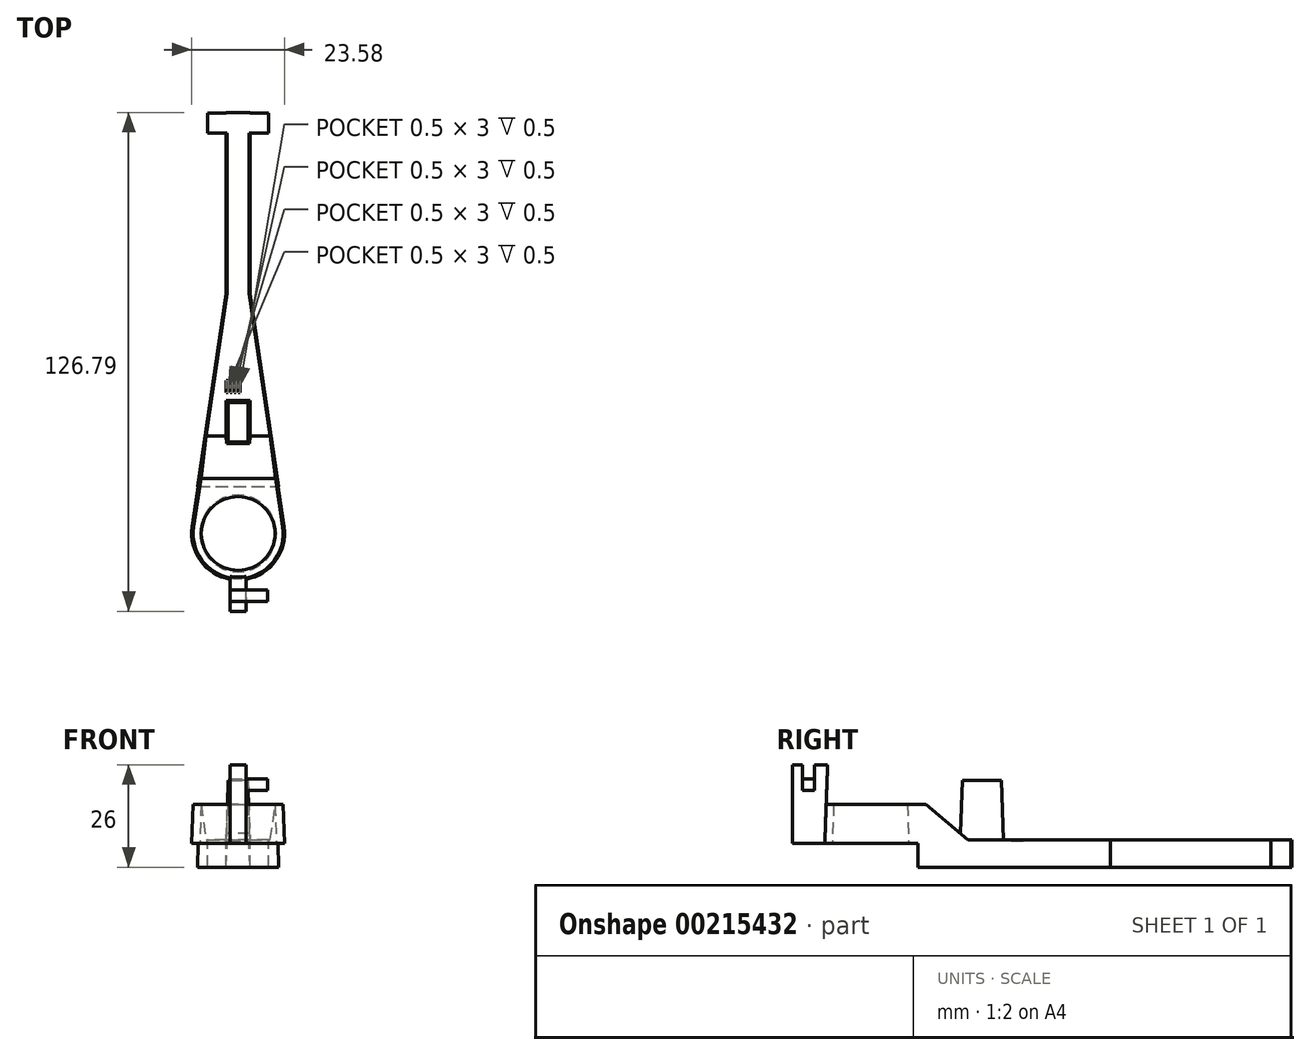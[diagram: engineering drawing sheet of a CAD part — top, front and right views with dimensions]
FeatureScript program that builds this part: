
annotation { "Feature Type Name" : "Feature", "Feature Type Description" : "" }
export const myFeature = defineFeature(function(context is Context, id is Id, definition is map)
    precondition{}
    {
        {
            var Q0;
            Q0=qCreatedBy(makeId("Top.planeOp"),FACE);
            var sketch = newSketch(context, id + "F0", { "sketchPlane" : qUnion([Q0])});
            skCircle(sketch, "E0", {"center": v(0, 0) * mm, "radius": 12 * mm});
            skLineSegment(sketch, "E1", {"start": v(-3, 95) * mm, "end": v(3, 95) * mm});
            skLineSegment(sketch, "E2", {"start": v(0, -12) * mm, "end": v(0, 95) * mm, "construction": true});
            skPoint(sketch, "E3", {"position": v(0, 95) * mm});
            skLineSegment(sketch, "E4", {"start": v(-3, 95) * mm, "end": v(-3, 61) * mm});
            skLineSegment(sketch, "E5", {"start": v(3, 95) * mm, "end": v(3, 61) * mm});
            skLineSegment(sketch, "E6", {"start": v(-3, 61) * mm, "end": v(-11.87, 1.78) * mm});
            skLineSegment(sketch, "E7", {"start": v(3, 61) * mm, "end": v(11.87, 1.78) * mm});
            skSolve(sketch);
        }
        {
            var Q0;
            Q0=qSketchRegion(id+"F0",true);
            extrude(context, id + "F1", {"entities" : qUnion([Q0]), "depth" : 16 * mm, "hasDraft" : true, "draftAngle" : 2 * degree, "draftPullDirection" : true});
        }
        {
            var Q0;
            Q0=qCreatedBy(makeId("Right.planeOp"),FACE);
            cPlane(context, id + "F2", {"entities" : qUnion([Q0]), "cplaneType" : CPlaneType.OFFSET, "offset" : 12 * mm, "width" : 150 * mm, "height" : 150 * mm});
        }
        {
            var Q0;
            Q0=qCreatedBy(id+"F2.planeOp",FACE);
            var sketch = newSketch(context, id + "F3", { "sketchPlane" : qUnion([Q0])});
            skLineSegment(sketch, "E8", {"start": v(94.76, 7) * mm, "end": v(24.76, 7) * mm});
            skLineSegment(sketch, "E9", {"start": v(24.76, 7) * mm, "end": v(14.03, 16) * mm});
            skLineSegment(sketch, "E10", {"start": v(12, 0) * mm, "end": v(12, 6) * mm});
            skLineSegment(sketch, "E11", {"start": v(12, 6) * mm, "end": v(-11.8, 6) * mm});
            skLineSegment(sketch, "E12", {"start": v(12, 0) * mm, "end": v(-12, 0) * mm});
            skLineSegment(sketch, "E13", {"start": v(-12, 0) * mm, "end": v(-11.8, 6) * mm});
            skLineSegment(sketch, "E14", {"start": v(14.03, 16) * mm, "end": v(94.44, 16) * mm});
            skLineSegment(sketch, "E15", {"start": v(94.44, 16) * mm, "end": v(94.76, 7) * mm});
            skSolve(sketch);
        }
        {
            var Q0;
            Q0=qSketchRegion(id+"F3",true);
            extrude(context, id + "F4", {"entities" : qUnion([Q0]), "operationType" : NewBodyOperationType.REMOVE, "endBound" : BoundingType.THROUGH_ALL, "oppositeDirection" : true, "depth" : 25 * mm});
        }
        {
            var Q0;
            Q0=makeQuery(id+"F4.boolean.opBoolean","COPY",FACE,{"derivedFrom":makeQuery(id+"F4.opExtrude","SWEPT_FACE",FACE,{"disambiguationData":[OSD([sQuery(id+"F3.wireOp",EDGE,"E8")])]})});
            cPlane(context, id + "F5", {"entities" : qUnion([Q0]), "cplaneType" : CPlaneType.OFFSET, "offset" : 15 * mm, "width" : 150 * mm, "height" : 150 * mm});
        }
        {
            var Q0;
            Q0=qCreatedBy(id+"F5.planeOp",FACE);
            var sketch = newSketch(context, id + "F6", { "sketchPlane" : qUnion([Q0])});
            skLineSegment(sketch, "E16.bottom", {"start": v(-2.5, 23.3) * mm, "end": v(2.5, 23.3) * mm});
            skLineSegment(sketch, "E16.top", {"start": v(-2.5, 33.3) * mm, "end": v(2.5, 33.3) * mm});
            skLineSegment(sketch, "E16.left", {"start": v(-2.5, 23.3) * mm, "end": v(-2.5, 33.3) * mm});
            skLineSegment(sketch, "E16.right", {"start": v(2.5, 23.3) * mm, "end": v(2.5, 33.3) * mm});
            skPoint(sketch, "E16.middle", {"position": v(0, 28.3) * mm});
            skSolve(sketch);
        }
        {
            var Q0;
            Q0=qSketchRegion(id+"F6",true);
            extrude(context, id + "F7", {"entities" : qUnion([Q0]), "operationType" : NewBodyOperationType.ADD, "endBound" : BoundingType.UP_TO_NEXT, "oppositeDirection" : true, "depth" : 25 * mm, "hasDraft" : true, "draftAngle" : 2 * degree});
        }
        {
            var Q0;
            Q0=makeQuery(id+"F4.boolean.opBoolean","COPY",FACE,{"derivedFrom":makeQuery(id+"F4.opExtrude","SWEPT_FACE",FACE,{"disambiguationData":[OSD([sQuery(id+"F3.wireOp",EDGE,"E11")])]})});
            var sketch = newSketch(context, id + "F8", { "sketchPlane" : qUnion([Q0])});
            skCircle(sketch, "E17", {"center": v(0, 0) * mm, "radius": 9.72 * mm});
            skSolve(sketch);
        }
        {
            var Q0;
            Q0=qSketchRegion(id+"F8",true);
            extrude(context, id + "F9", {"entities" : qUnion([Q0]), "operationType" : NewBodyOperationType.REMOVE, "endBound" : BoundingType.THROUGH_ALL, "oppositeDirection" : true, "depth" : 25 * mm, "hasDraft" : true, "draftAngle" : 2 * degree, "draftPullDirection" : true});
        }
        {
            var Q0;
            Q0=makeQuery(id+"F4.boolean.opBoolean","COPY",FACE,{"derivedFrom":makeQuery(id+"F4.opExtrude","SWEPT_FACE",FACE,{"disambiguationData":[OSD([sQuery(id+"F3.wireOp",EDGE,"E11")])]})});
            var sketch = newSketch(context, id + "F10", { "sketchPlane" : qUnion([Q0])});
            skLineSegment(sketch, "E18", {"start": v(0, 11.8) * mm, "end": v(0, 19.8) * mm, "construction": true});
            skPoint(sketch, "E18.endSnap0", {"position": v(0, 11.8) * mm});
            skLineSegment(sketch, "E19", {"start": v(0, 19.8) * mm, "end": v(-2, 19.8) * mm});
            skLineSegment(sketch, "E20", {"start": v(-2, 19.8) * mm, "end": v(-2, 11.62) * mm});
            skLineSegment(sketch, "E21", {"start": v(0, 19.8) * mm, "end": v(2, 19.8) * mm});
            skLineSegment(sketch, "E22", {"start": v(2, 19.8) * mm, "end": v(2, 11.62) * mm});
            skArc(sketch, "E23", {"start": v(2, 11.62) * mm, "mid": v(0, 11.8) * mm, "end": v(-2, 11.62) * mm});
            skSolve(sketch);
        }
        {
            var Q0;
            Q0=qCreatedBy(makeId("Front.planeOp"),FACE);
            var Q1;
            Q1=sQuery(id+"F10.wireOp",VERTEX,"E21.start");
            cPlane(context, id + "F11", {"entities" : qUnion([Q0, Q1]), "cplaneType" : CPlaneType.PLANE_POINT, "offset" : 25 * mm, "width" : 150 * mm, "height" : 150 * mm});
        }
        {
            var Q0;
            Q0=qCreatedBy(id+"F11.planeOp",FACE);
            var sketch = newSketch(context, id + "F12", { "sketchPlane" : qUnion([Q0])});
            skLineSegment(sketch, "E24.bottom", {"start": v(-2, 6) * mm, "end": v(2, 6) * mm});
            skLineSegment(sketch, "E24.top", {"start": v(-2, 26) * mm, "end": v(2, 26) * mm});
            skLineSegment(sketch, "E24.left", {"start": v(-2, 6) * mm, "end": v(-2, 26) * mm});
            skLineSegment(sketch, "E24.right", {"start": v(2, 6) * mm, "end": v(2, 26) * mm});
            skSolve(sketch);
        }
        {
            var Q0;
            Q0=qSketchRegion(id+"F12",true);
            var Q1;
            Q1=makeQuery(id+"F1.opExtrude","SWEPT_FACE",FACE,{"disambiguationData":[OSD([sQuery(id+"F0.wireOp",EDGE,"E0")])]});
            extrude(context, id + "F13", {"entities" : qUnion([Q0]), "operationType" : NewBodyOperationType.ADD, "endBound" : BoundingType.UP_TO_SURFACE, "oppositeDirection" : true, "endBoundEntityFace" : qUnion([Q1]), "depth" : 8 * mm});
        }
        {
            var Q0;
            Q0=makeQuery(id+"F13.opExtrude","SWEPT_FACE",FACE,{"disambiguationData":[OSD([sQuery(id+"F12.wireOp",EDGE,"E24.right")])]});
            var sketch = newSketch(context, id + "F14", { "sketchPlane" : qUnion([Q0])});
            skLineSegment(sketch, "E25.bottom", {"start": v(-17.3, 22.5) * mm, "end": v(-14.3, 22.5) * mm});
            skLineSegment(sketch, "E25.top", {"start": v(-17.3, 19.5) * mm, "end": v(-14.3, 19.5) * mm});
            skLineSegment(sketch, "E25.left", {"start": v(-17.3, 22.5) * mm, "end": v(-17.3, 19.5) * mm});
            skLineSegment(sketch, "E25.right", {"start": v(-14.3, 22.5) * mm, "end": v(-14.3, 19.5) * mm});
            skSolve(sketch);
        }
        {
            var Q0;
            Q0=qSketchRegion(id+"F14",true);
            extrude(context, id + "F15", {"entities" : qUnion([Q0]), "operationType" : NewBodyOperationType.ADD, "depth" : 5.5 * mm});
        }
        {
            var Q0;
            Q0=makeQuery(id+"F13.opExtrude","SWEPT_FACE",FACE,{"disambiguationData":[OSD([sQuery(id+"F12.wireOp",EDGE,"E24.right")])]});
            var sketch = newSketch(context, id + "F16", { "sketchPlane" : qUnion([Q0])});
            skLineSegment(sketch, "E26.bottom", {"start": v(-17.3, 22.5) * mm, "end": v(-14.3, 22.5) * mm});
            skLineSegment(sketch, "E26.top", {"start": v(-17.3, 26) * mm, "end": v(-14.3, 26) * mm});
            skLineSegment(sketch, "E26.left", {"start": v(-17.3, 22.5) * mm, "end": v(-17.3, 26) * mm});
            skLineSegment(sketch, "E26.right", {"start": v(-14.3, 22.5) * mm, "end": v(-14.3, 26) * mm});
            skSolve(sketch);
        }
        {
            var Q0;
            Q0=qSketchRegion(id+"F16",true);
            extrude(context, id + "F17", {"entities" : qUnion([Q0]), "operationType" : NewBodyOperationType.REMOVE, "endBound" : BoundingType.THROUGH_ALL, "oppositeDirection" : true, "depth" : 25 * mm});
        }
        {
            var Q0;
            Q0=makeQuery(id+"F4.boolean.opBoolean","COPY",FACE,{"derivedFrom":makeQuery(id+"F4.opExtrude","SWEPT_FACE",FACE,{"disambiguationData":[OSD([sQuery(id+"F3.wireOp",EDGE,"E8")])]})});
            var sketch = newSketch(context, id + "F18", { "sketchPlane" : qUnion([Q0])});
            skLineSegment(sketch, "E27.bottom", {"start": v(-3.02, 38.82) * mm, "end": v(-2.52, 38.82) * mm});
            skLineSegment(sketch, "E27.top", {"start": v(-3.02, 35.82) * mm, "end": v(-2.52, 35.82) * mm});
            skLineSegment(sketch, "E27.left", {"start": v(-3.02, 38.82) * mm, "end": v(-3.02, 35.82) * mm});
            skLineSegment(sketch, "E27.right", {"start": v(-2.52, 38.82) * mm, "end": v(-2.52, 35.82) * mm});
            skLineSegment(sketch, "E28.1.0.0", {"start": v(-1.52, 38.82) * mm, "end": v(-1.52, 35.82) * mm});
            skLineSegment(sketch, "E28.1.0.1", {"start": v(-2.02, 38.82) * mm, "end": v(-1.52, 38.82) * mm});
            skLineSegment(sketch, "E28.1.0.2", {"start": v(-2.02, 38.82) * mm, "end": v(-2.02, 35.82) * mm});
            skLineSegment(sketch, "E28.1.0.3", {"start": v(-2.02, 35.82) * mm, "end": v(-1.52, 35.82) * mm});
            skLineSegment(sketch, "E28.2.0.0", {"start": v(-0.52, 38.82) * mm, "end": v(-0.52, 35.82) * mm});
            skLineSegment(sketch, "E28.2.0.1", {"start": v(-1.02, 38.82) * mm, "end": v(-0.52, 38.82) * mm});
            skLineSegment(sketch, "E28.2.0.2", {"start": v(-1.02, 38.82) * mm, "end": v(-1.02, 35.82) * mm});
            skLineSegment(sketch, "E28.2.0.3", {"start": v(-1.02, 35.82) * mm, "end": v(-0.52, 35.82) * mm});
            skLineSegment(sketch, "E28.3.0.0", {"start": v(0.48, 38.82) * mm, "end": v(0.48, 35.82) * mm});
            skLineSegment(sketch, "E28.3.0.1", {"start": v(-0.02, 38.82) * mm, "end": v(0.48, 38.82) * mm});
            skLineSegment(sketch, "E28.3.0.2", {"start": v(-0.02, 38.82) * mm, "end": v(-0.02, 35.82) * mm});
            skLineSegment(sketch, "E28.3.0.3", {"start": v(-0.02, 35.82) * mm, "end": v(0.48, 35.82) * mm});
            skLineSegment(sketch, "E28.direction1", {"start": v(-2.52, 35.82) * mm, "end": v(-1.52, 35.82) * mm, "construction": true});
            skSolve(sketch);
        }
        {
            var Q0;
            Q0=qSketchRegion(id+"F18",true);
            extrude(context, id + "F19", {"entities" : qUnion([Q0]), "operationType" : NewBodyOperationType.REMOVE, "oppositeDirection" : true, "depth" : 0.5 * mm});
        }
        {
            var Q0;
            Q0=makeQuery(id+"F4.boolean.opBoolean","COPY",FACE,{"derivedFrom":makeQuery(id+"F4.opExtrude","SWEPT_FACE",FACE,{"disambiguationData":[OSD([sQuery(id+"F3.wireOp",EDGE,"E8")])]})});
            var sketch = newSketch(context, id + "F20", { "sketchPlane" : qUnion([Q0])});
            skLineSegment(sketch, "E29", {"start": v(-2.76, 94.76) * mm, "end": v(3.66, 94.76) * mm});
            skLineSegment(sketch, "E30", {"start": v(3.66, 94.76) * mm, "end": v(3.66, 95.22) * mm});
            skLineSegment(sketch, "E31", {"start": v(3.66, 95.22) * mm, "end": v(-3.37, 95.22) * mm});
            skLineSegment(sketch, "E32", {"start": v(-3.37, 95.22) * mm, "end": v(-3.37, 94.76) * mm});
            skLineSegment(sketch, "E33", {"start": v(-3.37, 94.76) * mm, "end": v(-2.76, 94.76) * mm});
            skSolve(sketch);
        }
        {
            var Q0;
            Q0 = qSketchRegion(id + "F20", true);
            extrude(context, id + "F21", {"entities" : qUnion([Q0]), "operationType" : NewBodyOperationType.REMOVE, "endBound" : BoundingType.THROUGH_ALL, "oppositeDirection" : true, "depth" : 25 * mm});
        }
        {
            var Q0;
            Q0=makeQuery(id+"F21.boolean.opBoolean","COPY",FACE,{"derivedFrom":makeQuery(id+"F21.opExtrude","SWEPT_FACE",FACE,{"disambiguationData":[OSD([sQuery(id+"F20.wireOp",EDGE,"E29"),sQuery(id+"F20.wireOp",EDGE,"E33")])]})});
            var sketch = newSketch(context, id + "F22", { "sketchPlane" : qUnion([Q0])});
            skLineSegment(sketch, "E34", {"start": v(-2.76, 7) * mm, "end": v(2.76, 7) * mm});
            skLineSegment(sketch, "E35", {"start": v(2.76, 7) * mm, "end": v(3, 0) * mm});
            skLineSegment(sketch, "E36", {"start": v(3, 0) * mm, "end": v(-3, 0) * mm});
            skLineSegment(sketch, "E37", {"start": v(-3, 0) * mm, "end": v(-2.76, 7) * mm});
            skSolve(sketch);
        }
        {
            var Q0;
            Q0 = qSketchRegion(id + "F22", true);
            extrude(context, id + "F23", {"entities" : qUnion([Q0]), "operationType" : NewBodyOperationType.ADD, "depth" : 12 * mm});
        }
        {
            var Q0;
            Q0=makeQuery(id+"F4.boolean.opBoolean","COPY",FACE,{"derivedFrom":makeQuery(id+"F4.opExtrude","SWEPT_FACE",FACE,{"disambiguationData":[OSD([sQuery(id+"F3.wireOp",EDGE,"E8")])]})});
            var sketch = newSketch(context, id + "F24", { "sketchPlane" : qUnion([Q0])});
            skLineSegment(sketch, "E38", {"start": v(0, 107) * mm, "end": v(0, 97) * mm, "construction": true});
            skLineSegment(sketch, "E39", {"start": v(-3, 107) * mm, "end": v(-4.75, 107) * mm});
            skLineSegment(sketch, "E40", {"start": v(-7.75, 106.76) * mm, "end": v(-7.75, 101.76) * mm});
            skLineSegment(sketch, "E41", {"start": v(-7.75, 101.76) * mm, "end": v(-3, 101.76) * mm});
            skLineSegment(sketch, "E42", {"start": v(-3, 106.76) * mm, "end": v(-3, 101.76) * mm});
            skLineSegment(sketch, "E43", {"start": v(-3, 101.76) * mm, "end": v(-3, 101.76) * mm});
            skLineSegment(sketch, "E44", {"start": v(-3, 106.76) * mm, "end": v(0, 106.76) * mm});
            skLineSegment(sketch, "E45", {"start": v(-4.75, 107) * mm, "end": v(0, 107) * mm});
            skPoint(sketch, "E46.orphan", {"position": v(-3, 107) * mm});
            skLineSegment(sketch, "E47", {"start": v(-3, 106.76) * mm, "end": v(-7.75, 106.76) * mm});
            skLineSegment(sketch, "E48", {"start": v(-3, 107) * mm, "end": v(-3, 106.76) * mm});
            skPoint(sketch, "E49.orphan", {"position": v(-7.75, 107) * mm});
            skLineSegment(sketch, "E50.MirrorCS", {"start": v(4.75, 107) * mm, "end": v(0, 107) * mm});
            skLineSegment(sketch, "E51.MirrorCS", {"start": v(3, 107) * mm, "end": v(4.75, 107) * mm});
            skPoint(sketch, "E52.MirrorP", {"position": v(3, 107) * mm});
            skLineSegment(sketch, "E53.MirrorCS", {"start": v(3, 107) * mm, "end": v(3, 106.76) * mm});
            skLineSegment(sketch, "E54.MirrorCS", {"start": v(3, 106.76) * mm, "end": v(0, 106.76) * mm});
            skLineSegment(sketch, "E55.MirrorCS", {"start": v(3, 106.76) * mm, "end": v(7.75, 106.76) * mm});
            skLineSegment(sketch, "E56.MirrorCS", {"start": v(3, 106.76) * mm, "end": v(3, 101.76) * mm});
            skLineSegment(sketch, "E57.MirrorCS", {"start": v(7.75, 101.76) * mm, "end": v(3, 101.76) * mm});
            skLineSegment(sketch, "E58.MirrorCS", {"start": v(7.75, 106.76) * mm, "end": v(7.75, 101.76) * mm});
            skLineSegment(sketch, "E59.MirrorCS", {"start": v(3, 101.76) * mm, "end": v(3, 101.76) * mm});
            skLineSegment(sketch, "E60", {"start": v(-3, 101.76) * mm, "end": v(-2.76, 101.76) * mm});
            skLineSegment(sketch, "E61", {"start": v(-2.76, 101.76) * mm, "end": v(-2.76, 106.76) * mm});
            skLineSegment(sketch, "E62", {"start": v(3, 101.76) * mm, "end": v(2.76, 101.76) * mm});
            skLineSegment(sketch, "E63", {"start": v(2.76, 101.76) * mm, "end": v(2.76, 106.76) * mm});
            skSolve(sketch);
        }
        {
            var Q0;
            Q0=makeQuery(id+"F24.imprint","IMPRINT",FACE,{"disambiguationData":[TD([[makeQuery(id+"F24.imprint","IMPRINT",EDGE,{"derivedFrom":sQuery(id+"F24.wireOp",EDGE,"E40")}),1.0]])]});
            var Q1;
            {var subQ0=sQuery(id+"F24.wireOp",EDGE,"E42");Q1=makeQuery(id+"F24.imprint","IMPRINT",FACE,{"disambiguationData":[TD([[makeQuery(id+"F24.imprint","IMPRINT",EDGE,{"derivedFrom":subQ0}),1.0]])]});}
            var Q2;
            {var subQ2=sQuery(id+"F24.wireOp",EDGE,"E56.MirrorCS");Q2=makeQuery(id+"F24.imprint","IMPRINT",FACE,{"disambiguationData":[TD([[makeQuery(id+"F24.imprint","IMPRINT",EDGE,{"derivedFrom":subQ2}),-1.0]])]});}
            var Q3;
            Q3=makeQuery(id+"F24.imprint","IMPRINT",FACE,{"disambiguationData":[TD([[makeQuery(id+"F24.imprint","IMPRINT",EDGE,{"derivedFrom":sQuery(id+"F24.wireOp",EDGE,"E55.MirrorCS")}),-1.0]])]});
            var Q4;
            {var subQ3=sQuery(id+"F24.wireOp",EDGE,"E48");Q4=makeQuery(id+"F24.imprint","IMPRINT",FACE,{"disambiguationData":[TD([[makeQuery(id+"F24.imprint","IMPRINT",EDGE,{"derivedFrom":subQ3}),1.0]])]});}
            var Q5;
            Q5=makeQuery(id+"F23.boolean.opBoolean","MERGE",FACE,{"derivedFrom":[makeQuery(id+"F1.opExtrude","CAP_FACE",FACE,{"disambiguationData":[OSD([sQuery(id+"F0.wireOp",EDGE,"E0"),sQuery(id+"F0.wireOp",EDGE,"E1"),sQuery(id+"F0.wireOp",EDGE,"E4"),sQuery(id+"F0.wireOp",EDGE,"E5"),sQuery(id+"F0.wireOp",EDGE,"E6"),sQuery(id+"F0.wireOp",EDGE,"E7")])],"isStart":true}),makeQuery(id+"F23.opExtrude","SWEPT_FACE",FACE,{"disambiguationData":[OSD([sQuery(id+"F22.wireOp",EDGE,"E36")])]})]});
            extrude(context, id + "F25", {"entities" : qUnion([Q0, Q1, Q2, Q3, Q4]), "operationType" : NewBodyOperationType.ADD, "endBound" : BoundingType.UP_TO_SURFACE, "oppositeDirection" : true, "endBoundEntityFace" : qUnion([Q5]), "depth" : 25 * mm});
        }
    });
